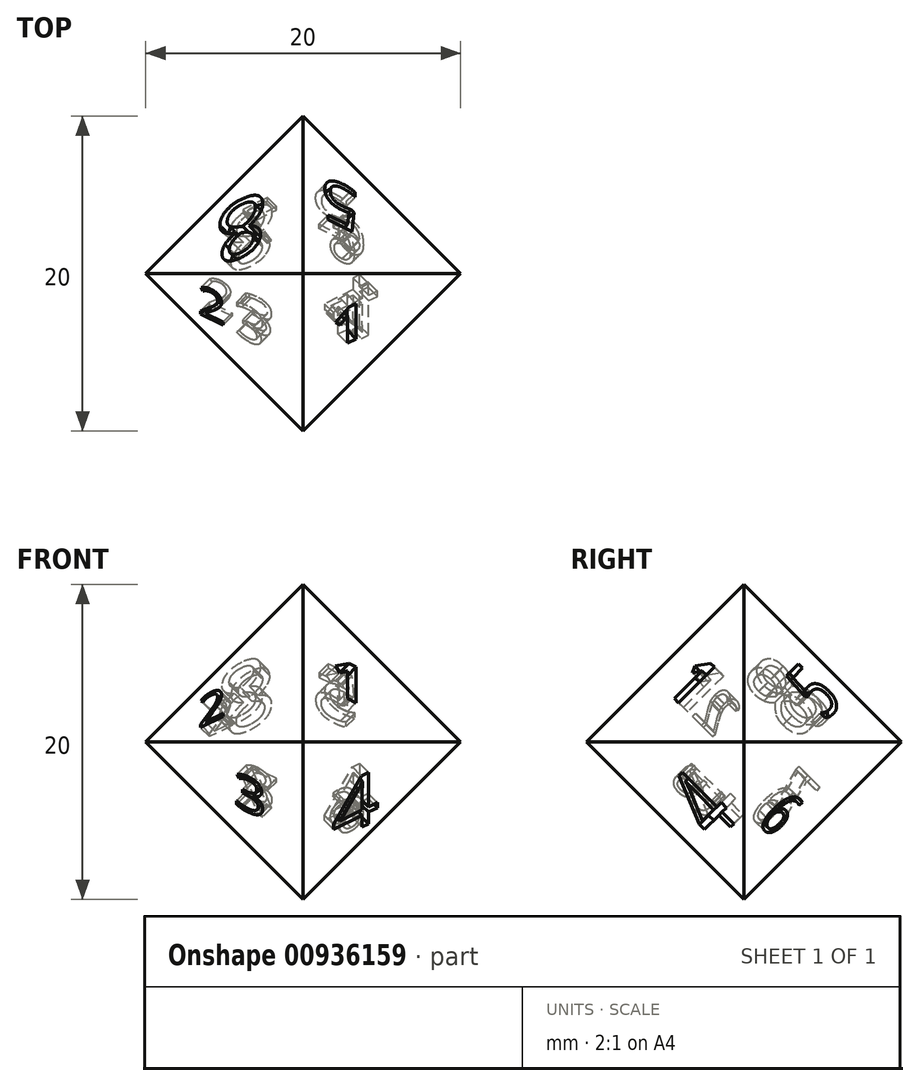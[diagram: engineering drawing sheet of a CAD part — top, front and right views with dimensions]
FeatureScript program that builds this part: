
annotation { "Feature Type Name" : "Feature", "Feature Type Description" : "" }
export const myFeature = defineFeature(function(context is Context, id is Id, definition is map)
    precondition{}
    {
        {
            var Q0;
            Q0=qCreatedBy(makeId("Top.planeOp"),FACE);
            var sketch = newSketch(context, id + "F0", { "sketchPlane" : qUnion([Q0])});
            skCircle(sketch, "E0.cCircle", {"center": v(0, 0) * mm, "radius": 10 * mm, "construction": true});
            skLineSegment(sketch, "E0.0", {"start": v(10, -10) * mm, "end": v(-10, -10) * mm});
            skLineSegment(sketch, "E0.1", {"start": v(-10, -10) * mm, "end": v(-10, 10) * mm});
            skLineSegment(sketch, "E0.2", {"start": v(-10, 10) * mm, "end": v(10, 10) * mm});
            skLineSegment(sketch, "E0.3", {"start": v(10, 10) * mm, "end": v(10, -10) * mm});
            skPoint(sketch, "E0.0.midPoint", {"position": v(0, -10) * mm});
            skSolve(sketch);
        }
        {
            var Q0;
            Q0=makeQuery(id+"F0.imprint","IMPRINT",FACE,{"disambiguationData":[TD([[makeQuery(id+"F0.imprint","IMPRINT",EDGE,{"derivedFrom":sQuery(id+"F0.wireOp",EDGE,"E0.0")}),-1.0]])]});
            extrude(context, id + "F1", {"entities" : qUnion([Q0]), "depth" : 20 * mm, "offsetDistance" : 25 * mm});
        }
        {
            var Q0;
            Q0=makeQuery(id+"F1.opExtrude","SWEPT_EDGE",EDGE,{"disambiguationData":[OSD([sQuery(id+"F0.wireOp",EDGE,"E0.1"),sQuery(id+"F0.wireOp",EDGE,"E0.2")])]});
            var Q1;
            Q1=makeQuery(id+"F1.opExtrude","CAP_EDGE",EDGE,{"disambiguationData":[OSD([sQuery(id+"F0.wireOp",EDGE,"E0.2")])],"isStart":true});
            var Q2;
            Q2=makeQuery(id+"F1.opExtrude","CAP_EDGE",EDGE,{"disambiguationData":[OSD([sQuery(id+"F0.wireOp",EDGE,"E0.1")])],"isStart":true});
            var Q3;
            Q3=makeQuery(id+"F1.opExtrude","SWEPT_FACE",FACE,{"disambiguationData":[OSD([sQuery(id+"F0.wireOp",EDGE,"E0.1")])]});
            var Q4;
            Q4=makeQuery(id+"F1.opExtrude","CAP_EDGE",EDGE,{"disambiguationData":[OSD([sQuery(id+"F0.wireOp",EDGE,"E0.2")])],"isStart":false});
            var Q5;
            Q5=makeQuery(id+"F1.opExtrude","CAP_EDGE",EDGE,{"disambiguationData":[OSD([sQuery(id+"F0.wireOp",EDGE,"E0.0")])],"isStart":false});
            var Q6;
            Q6=makeQuery(id+"F1.opExtrude","SWEPT_EDGE",EDGE,{"disambiguationData":[OSD([sQuery(id+"F0.wireOp",EDGE,"E0.0"),sQuery(id+"F0.wireOp",EDGE,"E0.3")])]});
            var Q7;
            Q7=makeQuery(id+"F1.opExtrude","CAP_EDGE",EDGE,{"disambiguationData":[OSD([sQuery(id+"F0.wireOp",EDGE,"E0.0")])],"isStart":true});
            var Q8;
            Q8=makeQuery(id+"F1.opExtrude","CAP_EDGE",EDGE,{"disambiguationData":[OSD([sQuery(id+"F0.wireOp",EDGE,"E0.3")])],"isStart":false});
            var Q9;
            Q9=makeQuery(id+"F1.opExtrude","SWEPT_EDGE",EDGE,{"disambiguationData":[OSD([sQuery(id+"F0.wireOp",EDGE,"E0.2"),sQuery(id+"F0.wireOp",EDGE,"E0.3")])]});
            var Q10;
            Q10=makeQuery(id+"F1.opExtrude","CAP_EDGE",EDGE,{"disambiguationData":[OSD([sQuery(id+"F0.wireOp",EDGE,"E0.3")])],"isStart":true});
            chamfer(context, id + "F2", {"entities" : qUnion([Q0, Q1, Q2, Q3, Q4, Q5, Q6, Q7, Q8, Q9, Q10]), "width" : 10 * mm, "tangentPropagation" : true});
        }
        {
            var Q0;
            {var subQ0=sQuery(id+"F0.wireOp",EDGE,"E0.3");var subQ1=sQuery(id+"F0.wireOp",EDGE,"E0.0");Q0=makeQuery(id+"F2.opChamfer","BLEND_FACE",FACE,{"disambiguationData":[OSD([subQ1,subQ0]),TDD([makeQuery(id+"F1.opExtrude","CAP_VERTEX",VERTEX,{"disambiguationData":[OSD([subQ1,subQ0])],"isStart":false})])]});}
            var sketch = newSketch(context, id + "F3", { "sketchPlane" : qUnion([Q0])});
            skText(sketch, "E1", { "text": "1", "fontName": "OpenSans-Bold.ttf"});
            const initialGuessF3  = {"E1": [-0.0059, 0.0059, 1, 0, 0.00322]};
            skSetInitialGuess(sketch, initialGuessF3);
            skSolve(sketch);
        }
        {
            var Q0;
            Q0 = qSketchRegion(id + "F3", true);
            extrude(context, id + "F4", {"entities" : qUnion([Q0]), "operationType" : NewBodyOperationType.REMOVE, "oppositeDirection" : true, "depth" : 1 * mm, "offsetDistance" : 25 * mm});
        }
        {
            var Q0;
            {var subQ0=sQuery(id+"F0.wireOp",EDGE,"E0.1");var subQ1=sQuery(id+"F0.wireOp",EDGE,"E0.0");Q0=makeQuery(id+"F2.opChamfer","BLEND_FACE",FACE,{"disambiguationData":[OSD([subQ1,subQ0]),TDD([makeQuery(id+"F1.opExtrude","CAP_VERTEX",VERTEX,{"disambiguationData":[OSD([subQ1,subQ0])],"isStart":false})])]});}
            var sketch = newSketch(context, id + "F5", { "sketchPlane" : qUnion([Q0])});
            skText(sketch, "E2", { "text": "2\n", "fontName": "OpenSans-Regular.ttf"});
            const initialGuessF5  = {"E2": [0, 0.0059, 1, 0, 0.00268]};
            skSetInitialGuess(sketch, initialGuessF5);
            skSolve(sketch);
        }
        {
            var Q0;
            Q0 = qSketchRegion(id + "F5", true);
            extrude(context, id + "F6", {"entities" : qUnion([Q0]), "operationType" : NewBodyOperationType.REMOVE, "oppositeDirection" : true, "depth" : 1 * mm, "offsetDistance" : 25 * mm});
        }
        {
            var Q0;
            {var subQ0=sQuery(id+"F0.wireOp",EDGE,"E0.1");var subQ1=sQuery(id+"F0.wireOp",EDGE,"E0.0");Q0=makeQuery(id+"F2.opChamfer","BLEND_FACE",FACE,{"disambiguationData":[OSD([subQ1,subQ0]),TDD([makeQuery(id+"F1.opExtrude","CAP_VERTEX",VERTEX,{"disambiguationData":[OSD([subQ1,subQ0])],"isStart":true})])]});}
            var sketch = newSketch(context, id + "F7", { "sketchPlane" : qUnion([Q0])});
            skText(sketch, "E3", { "text": "3\n", "fontName": "OpenSans-Regular.ttf"});
            const initialGuessF7  = {"E3": [-0.00537, 0.00542, 1, 0, 0.00312]};
            skSetInitialGuess(sketch, initialGuessF7);
            skSolve(sketch);
        }
        {
            var Q0;
            Q0 = qSketchRegion(id + "F7", true);
            extrude(context, id + "F8", {"entities" : qUnion([Q0]), "operationType" : NewBodyOperationType.REMOVE, "oppositeDirection" : true, "depth" : 1 * mm, "offsetDistance" : 25 * mm});
        }
        {
            var Q0;
            {var subQ0=sQuery(id+"F0.wireOp",EDGE,"E0.3");var subQ1=sQuery(id+"F0.wireOp",EDGE,"E0.0");Q0=makeQuery(id+"F2.opChamfer","BLEND_FACE",FACE,{"disambiguationData":[OSD([subQ1,subQ0]),TDD([makeQuery(id+"F1.opExtrude","CAP_VERTEX",VERTEX,{"disambiguationData":[OSD([subQ1,subQ0])],"isStart":true})])]});}
            var sketch = newSketch(context, id + "F9", { "sketchPlane" : qUnion([Q0])});
            skText(sketch, "E4", { "text": "4\n", "fontName": "OpenSans-Regular.ttf"});
            const initialGuessF9  = {"E4": [0.00223, 0.00385, 1, 0, 0.00462]};
            skSetInitialGuess(sketch, initialGuessF9);
            skSolve(sketch);
        }
        {
            var Q0;
            Q0 = qSketchRegion(id + "F9", true);
            extrude(context, id + "F10", {"entities" : qUnion([Q0]), "operationType" : NewBodyOperationType.REMOVE, "oppositeDirection" : true, "depth" : 1 * mm, "offsetDistance" : 25 * mm});
        }
        {
            var Q0;
            {var subQ0=sQuery(id+"F0.wireOp",EDGE,"E0.3");var subQ1=sQuery(id+"F0.wireOp",EDGE,"E0.2");Q0=makeQuery(id+"F2.opChamfer","BLEND_FACE",FACE,{"disambiguationData":[OSD([subQ1,subQ0]),TDD([makeQuery(id+"F1.opExtrude","CAP_VERTEX",VERTEX,{"disambiguationData":[OSD([subQ1,subQ0])],"isStart":false})])]});}
            var sketch = newSketch(context, id + "F11", { "sketchPlane" : qUnion([Q0])});
            skText(sketch, "E5", { "text": "5\n", "fontName": "OpenSans-Regular.ttf"});
            const initialGuessF11  = {"E5": [0.00377, 0.00438, 1, 0, 0.0038]};
            skSetInitialGuess(sketch, initialGuessF11);
            skSolve(sketch);
        }
        {
            var Q0;
            {var subQ0=sQuery(id+"F0.wireOp",EDGE,"E0.3");var subQ1=sQuery(id+"F0.wireOp",EDGE,"E0.2");Q0=makeQuery(id+"F2.opChamfer","BLEND_FACE",FACE,{"disambiguationData":[OSD([subQ1,subQ0]),TDD([makeQuery(id+"F1.opExtrude","CAP_VERTEX",VERTEX,{"disambiguationData":[OSD([subQ1,subQ0])],"isStart":true})])]});}
            var sketch = newSketch(context, id + "F12", { "sketchPlane" : qUnion([Q0])});
            skText(sketch, "E6", { "text": "6\n", "fontName": "OpenSans-Regular.ttf"});
            const initialGuessF12  = {"E6": [-0.00495, 0.00405, 1, 0, 0.00295]};
            skSetInitialGuess(sketch, initialGuessF12);
            skSolve(sketch);
        }
        {
            var Q0;
            {var subQ0=sQuery(id+"F0.wireOp",EDGE,"E0.2");var subQ1=sQuery(id+"F0.wireOp",EDGE,"E0.1");Q0=makeQuery(id+"F2.opChamfer","BLEND_FACE",FACE,{"disambiguationData":[OSD([subQ1,subQ0]),TDD([makeQuery(id+"F1.opExtrude","CAP_VERTEX",VERTEX,{"disambiguationData":[OSD([subQ1,subQ0])],"isStart":true})])]});}
            var sketch = newSketch(context, id + "F13", { "sketchPlane" : qUnion([Q0])});
            skText(sketch, "E7", { "text": "7\n", "fontName": "OpenSans-Regular.ttf"});
            const initialGuessF13  = {"E7": [0.0026, 0.0056, 1, 0, 0.00286]};
            skSetInitialGuess(sketch, initialGuessF13);
            skSolve(sketch);
        }
        {
            var Q0;
            {var subQ0=sQuery(id+"F0.wireOp",EDGE,"E0.2");var subQ1=sQuery(id+"F0.wireOp",EDGE,"E0.1");Q0=makeQuery(id+"F2.opChamfer","BLEND_FACE",FACE,{"disambiguationData":[OSD([subQ1,subQ0]),TDD([makeQuery(id+"F1.opExtrude","CAP_VERTEX",VERTEX,{"disambiguationData":[OSD([subQ1,subQ0])],"isStart":false})])]});}
            var sketch = newSketch(context, id + "F14", { "sketchPlane" : qUnion([Q0])});
            skText(sketch, "E8", { "text": "8\n", "fontName": "OpenSans-Regular.ttf"});
            const initialGuessF14  = {"E8": [-0.00538, 0.00477, 1, 0, 0.00511]};
            skSetInitialGuess(sketch, initialGuessF14);
            skSolve(sketch);
        }
        {
            var Q0;
            Q0 = qSketchRegion(id + "F11", true);
            extrude(context, id + "F15", {"entities" : qUnion([Q0]), "operationType" : NewBodyOperationType.REMOVE, "oppositeDirection" : true, "depth" : 1 * mm, "offsetDistance" : 25 * mm});
        }
        {
            var Q0;
            Q0 = qSketchRegion(id + "F12", true);
            extrude(context, id + "F16", {"entities" : qUnion([Q0]), "operationType" : NewBodyOperationType.REMOVE, "oppositeDirection" : true, "depth" : 1 * mm, "offsetDistance" : 25 * mm});
        }
        {
            var Q0;
            Q0 = qSketchRegion(id + "F13", true);
            extrude(context, id + "F17", {"entities" : qUnion([Q0]), "operationType" : NewBodyOperationType.REMOVE, "oppositeDirection" : true, "depth" : 1 * mm, "offsetDistance" : 25 * mm});
        }
        {
            var Q0;
            Q0 = qSketchRegion(id + "F14", true);
            extrude(context, id + "F18", {"entities" : qUnion([Q0]), "operationType" : NewBodyOperationType.REMOVE, "oppositeDirection" : true, "depth" : 1 * mm, "offsetDistance" : 25 * mm});
        }
    });
